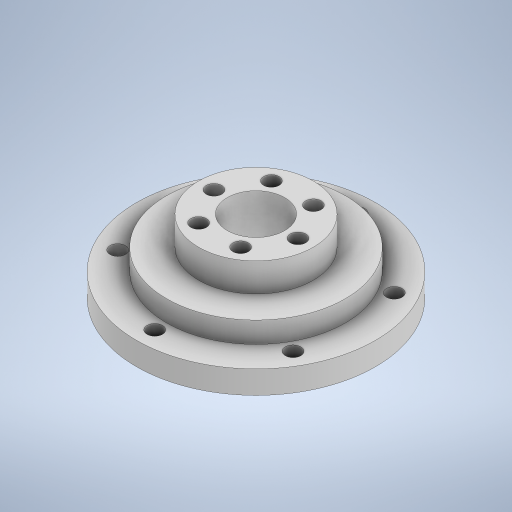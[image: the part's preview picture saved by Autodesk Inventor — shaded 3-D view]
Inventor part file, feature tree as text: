
AUTODESK INVENTOR PART (.ipt)
format: ipt  version: 2024 (Build 280153000, 153)  size: 346,112 bytes
history: native  units: mm
features: extrude x5, sketch x5, projected_geometry x3
ambient origin geometry x8: Origin, YZ Plane, XZ Plane, XY Plane, X Axis, Y Axis, Z Axis, Center Point
bodies: Solid1 (feature_tree)
feature tree (13):
  extrude  "Extrusion1"  Depth=106.0mm
  extrude  "Extrusion2"  Depth=12.0mm TaperAngle=0.0deg
  extrude  "Extrusion3"  Depth=8.0mm TaperAngle=0.0deg
  extrude  "Extrusion4"  Depth=8.1mm
  extrude  "Extrusion5"  Depth=11.0mm
  sketch  "Sketch1"  dims[d0=125.0mm d1=106.0mm]
  sketch  "Sketch2"  dims[d2=60.0mm d4=360.0deg d6=12.0mm d7=0.0mm]
  sketch  "Sketch3"  dims[d8=30.0mm d9=8.0mm d10=0.0mm]
  projected_geometry  "Projected Loop1"
  sketch  "Sketch4"  dims[d11=22.0mm d12=8.1mm]
  projected_geometry  "Projected Loop2"
  sketch  "Sketch5"  dims[d13=60.0mm d15=360.0deg d17=60.0mm d18=8.1mm d19=24.0mm d20=0.0mm d22=11.0mm d23=0.0mm d24=93.5mm d25=2.0mm d26=0.0mm]
  projected_geometry  "Projected Loop3"
